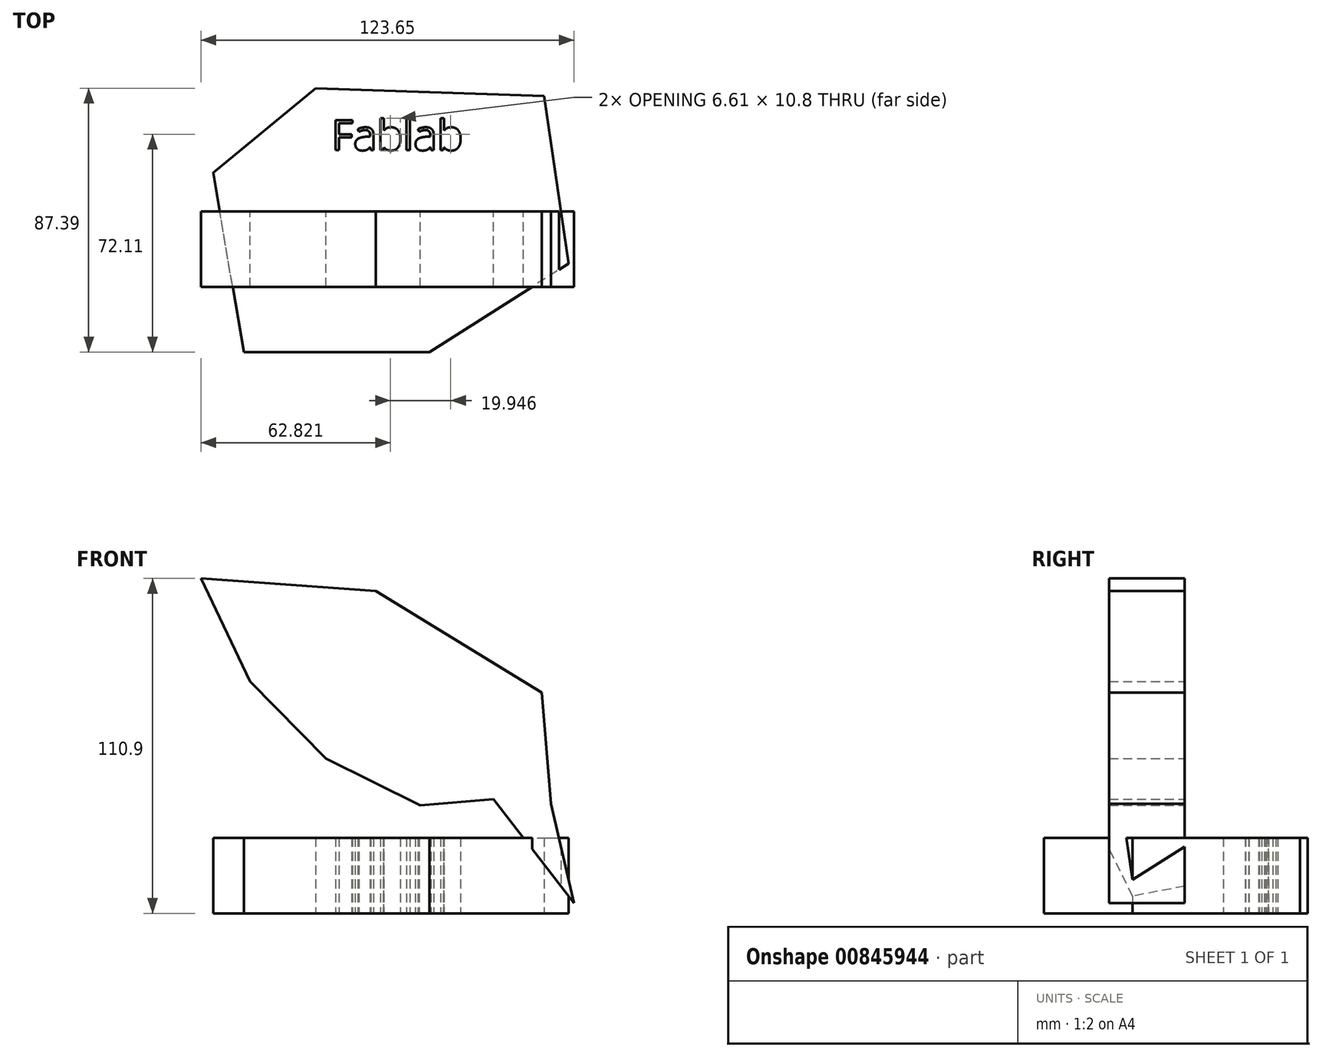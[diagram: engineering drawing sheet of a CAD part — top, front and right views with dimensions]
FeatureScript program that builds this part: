
annotation { "Feature Type Name" : "Feature", "Feature Type Description" : "" }
export const myFeature = defineFeature(function(context is Context, id is Id, definition is map)
    precondition{}
    {
        {
            var Q0;
            Q0=qCreatedBy(makeId("Top.planeOp"),FACE);
            var sketch = newSketch(context, id + "F0", { "sketchPlane" : qUnion([Q0])});
            skLineSegment(sketch, "E0", {"start": v(-37.66, 40.76) * mm, "end": v(37.99, 38.15) * mm});
            skLineSegment(sketch, "E1", {"start": v(37.99, 38.15) * mm, "end": v(46.14, -17.28) * mm});
            skLineSegment(sketch, "E2", {"start": v(46.14, -17.28) * mm, "end": v(-28.2, -14.35) * mm});
            skLineSegment(sketch, "E3", {"start": v(-28.2, -14.35) * mm, "end": v(-37.66, 40.76) * mm});
            skLineSegment(sketch, "E4", {"start": v(-28.2, -14.35) * mm, "end": v(-61.47, -46.63) * mm});
            skLineSegment(sketch, "E5", {"start": v(-61.47, -46.63) * mm, "end": v(-71.66, 12.76) * mm});
            skLineSegment(sketch, "E6", {"start": v(-71.66, 12.76) * mm, "end": v(-37.66, 40.76) * mm});
            skLineSegment(sketch, "E7", {"start": v(46.14, -17.28) * mm, "end": v(0, -46.63) * mm});
            skLineSegment(sketch, "E8", {"start": v(0, -46.63) * mm, "end": v(-61.47, -46.63) * mm});
            skLineSegment(sketch, "E9", {"start": v(0, -46.63) * mm, "end": v(-9.36, 7.94) * mm});
            skLineSegment(sketch, "E10", {"start": v(-9.36, 7.94) * mm, "end": v(37.99, 38.15) * mm});
            skLineSegment(sketch, "E11", {"start": v(-9.36, 7.94) * mm, "end": v(-71.66, 12.76) * mm});
            skText(sketch, "E12", { "text": "Fablab", "fontName": "OpenSans-Regular.ttf"});
            const initialGuessF0  = {"E12": [-0.03245, 0.02022, 1, 0, 0.0101]};
            skSetInitialGuess(sketch, initialGuessF0);
            skSolve(sketch);
        }
        {
            var Q0;
            {var subQ0=sQuery(id+"F0.wireOp",EDGE,"E7");Q0=makeQuery(id+"F0.imprint","IMPRINT",FACE,{"disambiguationData":[TD([[makeQuery(id+"F0.imprint","IMPRINT",EDGE,{"derivedFrom":subQ0}),-1.0]])]});}
            var Q1;
            {var subQ0=sQuery(id+"F0.wireOp",EDGE,"E6");Q1=makeQuery(id+"F0.imprint","IMPRINT",FACE,{"disambiguationData":[TD([[makeQuery(id+"F0.imprint","IMPRINT",EDGE,{"derivedFrom":subQ0}),-1.0]])]});}
            var Q2;
            {var subQ0=sQuery(id+"F0.wireOp",EDGE,"E1");Q2=makeQuery(id+"F0.imprint","IMPRINT",FACE,{"disambiguationData":[TD([[makeQuery(id+"F0.imprint","IMPRINT",EDGE,{"derivedFrom":subQ0}),-1.0]])]});}
            var Q3;
            {var subQ0=sQuery(id+"F0.wireOp",EDGE,"E4");Q3=makeQuery(id+"F0.imprint","IMPRINT",FACE,{"disambiguationData":[TD([[makeQuery(id+"F0.imprint","IMPRINT",EDGE,{"derivedFrom":subQ0}),1.0]])]});}
            var Q4;
            {var subQ0=sQuery(id+"F0.wireOp",EDGE,"E4");Q4=makeQuery(id+"F0.imprint","IMPRINT",FACE,{"disambiguationData":[TD([[makeQuery(id+"F0.imprint","IMPRINT",EDGE,{"derivedFrom":subQ0}),-1.0]])]});}
            var Q5;
            {var subQ0=sQuery(id+"F0.wireOp",EDGE,"E0");Q5=makeQuery(id+"F0.imprint","IMPRINT",FACE,{"disambiguationData":[TD([[makeQuery(id+"F0.imprint","IMPRINT",EDGE,{"derivedFrom":subQ0}),-1.0]])]});}
            var Q6;
            {var subQ1=sQuery(id+"F0.wireOp",EDGE,"E2");var subQ3=sQuery(id+"F0.wireOp",EDGE,"E9");var subQ4=makeQuery(id+"F0.imprint","INTERSECT",VERTEX,{"derivedFrom":[subQ1,subQ3]});Q6=makeQuery(id+"F0.imprint","IMPRINT",FACE,{"disambiguationData":[TD([[makeQuery(id+"F0.imprint","IMPRINT",EDGE,{"disambiguationData":[TD([[subQ4,-1.0]])],"derivedFrom":subQ1}),-1.0]])]});}
            extrude(context, id + "F1", {"entities" : qUnion([Q0, Q1, Q2, Q3, Q4, Q5, Q6]), "depth" : 25 * mm, "offsetDistance" : 25 * mm});
        }
        {
            var Q0;
            Q0=qCreatedBy(makeId("Front.planeOp"),FACE);
            var sketch = newSketch(context, id + "F2", { "sketchPlane" : qUnion([Q0])});
            skLineSegment(sketch, "E13", {"start": v(-75.72, 53.73) * mm, "end": v(-75.72, 110.9) * mm});
            skLineSegment(sketch, "E14", {"start": v(-75.72, 110.9) * mm, "end": v(-17.76, 106.74) * mm});
            skLineSegment(sketch, "E15", {"start": v(-17.76, 106.74) * mm, "end": v(-13.4, 55.35) * mm});
            skLineSegment(sketch, "E16", {"start": v(40.33, 36.23) * mm, "end": v(37.2, 73.16) * mm});
            skLineSegment(sketch, "E17", {"start": v(37.2, 73.16) * mm, "end": v(-17.76, 106.74) * mm});
            skLineSegment(sketch, "E18", {"start": v(-66.5, 17.13) * mm, "end": v(-59.36, 76.75) * mm});
            skLineSegment(sketch, "E19", {"start": v(-59.36, 76.75) * mm, "end": v(-75.72, 110.9) * mm});
            skLineSegment(sketch, "E20", {"start": v(-25.27, 0) * mm, "end": v(-34.24, 51.27) * mm});
            skLineSegment(sketch, "E21", {"start": v(-34.24, 51.27) * mm, "end": v(-59.36, 76.75) * mm});
            skLineSegment(sketch, "E22", {"start": v(0, 0) * mm, "end": v(-3.03, 35.74) * mm});
            skLineSegment(sketch, "E23", {"start": v(-3.03, 35.74) * mm, "end": v(-34.24, 51.27) * mm});
            skLineSegment(sketch, "E24", {"start": v(-3.03, 35.74) * mm, "end": v(21.2, 37.8) * mm});
            skLineSegment(sketch, "E25", {"start": v(21.2, 37.8) * mm, "end": v(47.93, 3.4) * mm});
            skLineSegment(sketch, "E26", {"start": v(47.93, 3.4) * mm, "end": v(40.33, 36.23) * mm});
            skSolve(sketch);
        }
        {
            var Q0;
            Q0 = qSketchRegion(id + "F2", true);
            extrude(context, id + "F3", {"entities" : qUnion([Q0]), "operationType" : NewBodyOperationType.ADD, "depth" : 25 * mm, "offsetDistance" : 25 * mm});
        }
    });
